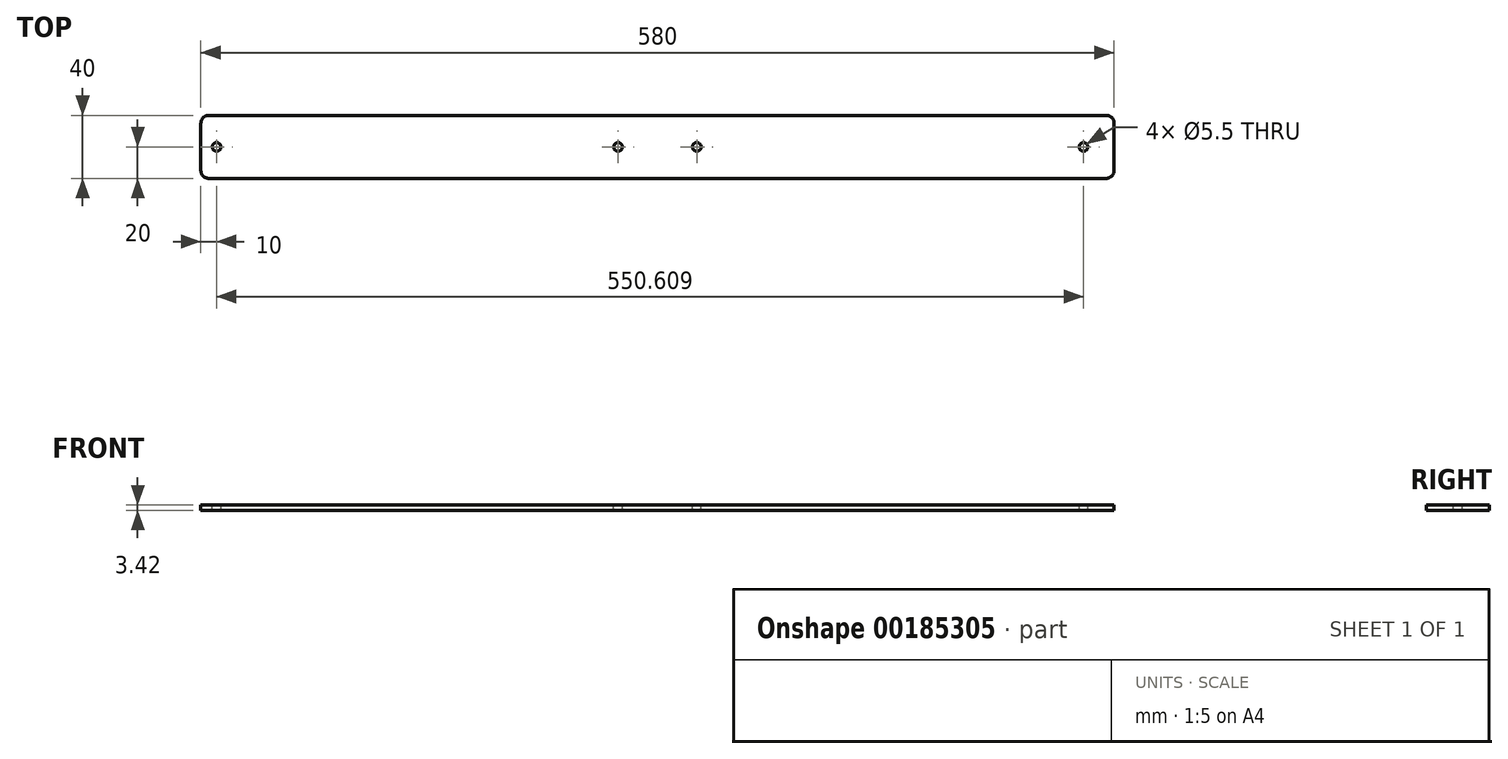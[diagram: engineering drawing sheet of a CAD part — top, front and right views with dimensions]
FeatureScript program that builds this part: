
annotation { "Feature Type Name" : "Feature", "Feature Type Description" : "" }
export const myFeature = defineFeature(function(context is Context, id is Id, definition is map)
    precondition{}
    {
        {
            var Q0;
            Q0=qCreatedBy(makeId("Top.planeOp"),FACE);
            var sketch = newSketch(context, id + "F0", { "sketchPlane" : qUnion([Q0])});
            skLineSegment(sketch, "E0.bottom", {"start": v(290, 20) * mm, "end": v(-290, 20) * mm});
            skLineSegment(sketch, "E0.top", {"start": v(290, -20) * mm, "end": v(-290, -20) * mm});
            skLineSegment(sketch, "E0.left", {"start": v(290, 20) * mm, "end": v(290, -20) * mm});
            skLineSegment(sketch, "E0.right", {"start": v(-290, 20) * mm, "end": v(-290, -20) * mm});
            skPoint(sketch, "E0.middle", {"position": v(0, 0) * mm});
            skSolve(sketch);
        }
        {
            var Q0;
            Q0 = qSketchRegion(id + "F0", true);
            extrude(context, id + "F1", {"entities" : qUnion([Q0]), "depth" : 3.42 * mm});
        }
        {
            var Q0;
            Q0=makeQuery(id+"F1.opExtrude","SWEPT_EDGE",EDGE,{"disambiguationData":[OSD([sQuery(id+"F0.wireOp",EDGE,"E0.bottom"),sQuery(id+"F0.wireOp",EDGE,"E0.right")])]});
            var Q1;
            Q1=makeQuery(id+"F1.opExtrude","SWEPT_EDGE",EDGE,{"disambiguationData":[OSD([sQuery(id+"F0.wireOp",EDGE,"E0.top"),sQuery(id+"F0.wireOp",EDGE,"E0.right")])]});
            var Q2;
            Q2=makeQuery(id+"F1.opExtrude","SWEPT_EDGE",EDGE,{"disambiguationData":[OSD([sQuery(id+"F0.wireOp",EDGE,"E0.bottom"),sQuery(id+"F0.wireOp",EDGE,"E0.left")])]});
            var Q3;
            Q3=makeQuery(id+"F1.opExtrude","SWEPT_EDGE",EDGE,{"disambiguationData":[OSD([sQuery(id+"F0.wireOp",EDGE,"E0.top"),sQuery(id+"F0.wireOp",EDGE,"E0.left")])]});
            fillet(context, id + "F2", {"entities" : qUnion([Q0, Q1, Q2, Q3]), "radius" : 5 * mm, "tangentPropagation" : true, "allowEdgeOverflow" : false});
        }
        {
            var Q0;
            Q0=makeQuery(id+"F1.opExtrude","CAP_FACE",FACE,{"disambiguationData":[OSD([sQuery(id+"F0.wireOp",EDGE,"E0.bottom"),sQuery(id+"F0.wireOp",EDGE,"E0.top"),sQuery(id+"F0.wireOp",EDGE,"E0.left"),sQuery(id+"F0.wireOp",EDGE,"E0.right")])],"isStart":false});
            var sketch = newSketch(context, id + "F3", { "sketchPlane" : qUnion([Q0])});
            skLineSegment(sketch, "E1", {"start": v(-280, 0) * mm, "end": v(-25, 0) * mm, "construction": true});
            skLineSegment(sketch, "E2", {"start": v(-25, 0) * mm, "end": v(25, 0) * mm, "construction": true});
            skLineSegment(sketch, "E3", {"start": v(25, 0) * mm, "end": v(270.6, 0) * mm, "construction": true});
            skSolve(sketch);
        }
        {
            var Q0;
            Q0=sQuery(id+"F3.wireOp",VERTEX,"E1.start");
            var Q1;
            Q1=sQuery(id+"F3.wireOp",VERTEX,"E2.start");
            var Q2;
            Q2=sQuery(id+"F3.wireOp",VERTEX,"E3.start");
            var Q3;
            Q3=sQuery(id+"F3.wireOp",VERTEX,"E3.end");
            var Q4;
            Q4=makeQuery(id+"F1.opExtrude","SWEPT_BODY",BODY,{"disambiguationData":[OSD([sQuery(id+"F0.wireOp",EDGE,"E0.bottom"),sQuery(id+"F0.wireOp",EDGE,"E0.top"),sQuery(id+"F0.wireOp",EDGE,"E0.left"),sQuery(id+"F0.wireOp",EDGE,"E0.right")])]});
            hole(context, id + "F4", {"style" : HoleStyle.SIMPLE, "endStyle" : HoleEndStyle.THROUGH, "standardTappedOrClearance" : lookupTablePath({ "standard" : "ISO", "fit" : "Normal", "size" : "M5", "type" : "Clearance" }), "standardBlindInLast" : lookupTablePath({ "fit" : "Standard", "standard" : "ISO", "size" : "M5", "type" : "Clearance" }), "holeDiameter" : 5.5 * mm, "locations" : qUnion([Q0, Q1, Q2, Q3]), "scope" : qUnion([Q4]), "isTappedThrough" : true});
        }
    });
